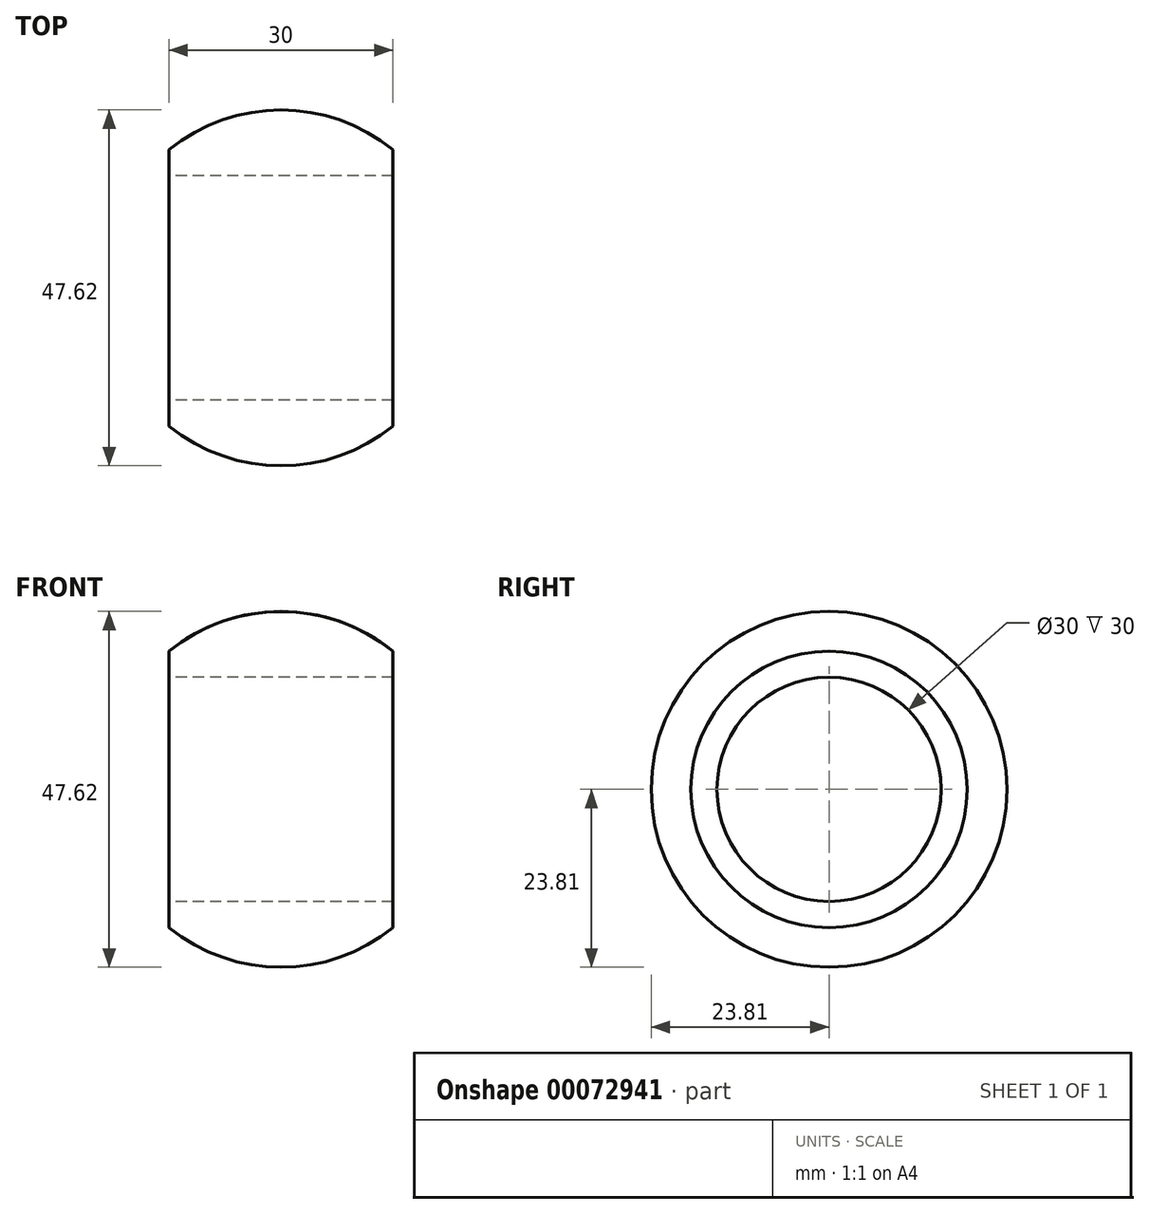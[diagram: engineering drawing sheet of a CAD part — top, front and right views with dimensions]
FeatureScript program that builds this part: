
annotation { "Feature Type Name" : "Feature", "Feature Type Description" : "" }
export const myFeature = defineFeature(function(context is Context, id is Id, definition is map)
    precondition{}
    {
        {
            var Q0;
            Q0=qCreatedBy(makeId("Top.planeOp"),FACE);
            var sketch = newSketch(context, id + "F0", { "sketchPlane" : qUnion([Q0])});
            skArc(sketch, "E0", {"start": v(15, 18.5) * mm, "mid": v(0, 23.81) * mm, "end": v(-15, 18.5) * mm});
            skLineSegment(sketch, "E1", {"start": v(-15, 18.5) * mm, "end": v(-15, 15) * mm});
            skLineSegment(sketch, "E2", {"start": v(-15, 15) * mm, "end": v(15, 15) * mm});
            skLineSegment(sketch, "E3", {"start": v(15, 15) * mm, "end": v(15, 18.5) * mm});
            skLineSegment(sketch, "E4", {"start": v(-84.64, 0) * mm, "end": v(103.3, 0) * mm, "construction": true});
            skSolve(sketch);
        }
        {
            var Q0;
            Q0=makeQuery(id+"F0.imprint","IMPRINT",FACE,{"disambiguationData":[TD([[makeQuery(id+"F0.imprint","IMPRINT",EDGE,{"derivedFrom":sQuery(id+"F0.wireOp",EDGE,"E0")}),1.0]])]});
            var Q1;
            Q1=sQuery(id+"F0.wireOp",EDGE,"E4");
            revolve(context, id + "F1", {"entities" : qUnion([Q0]), "axis" : qUnion([Q1]), "revolveType" : RevolveType.FULL});
        }
    });
